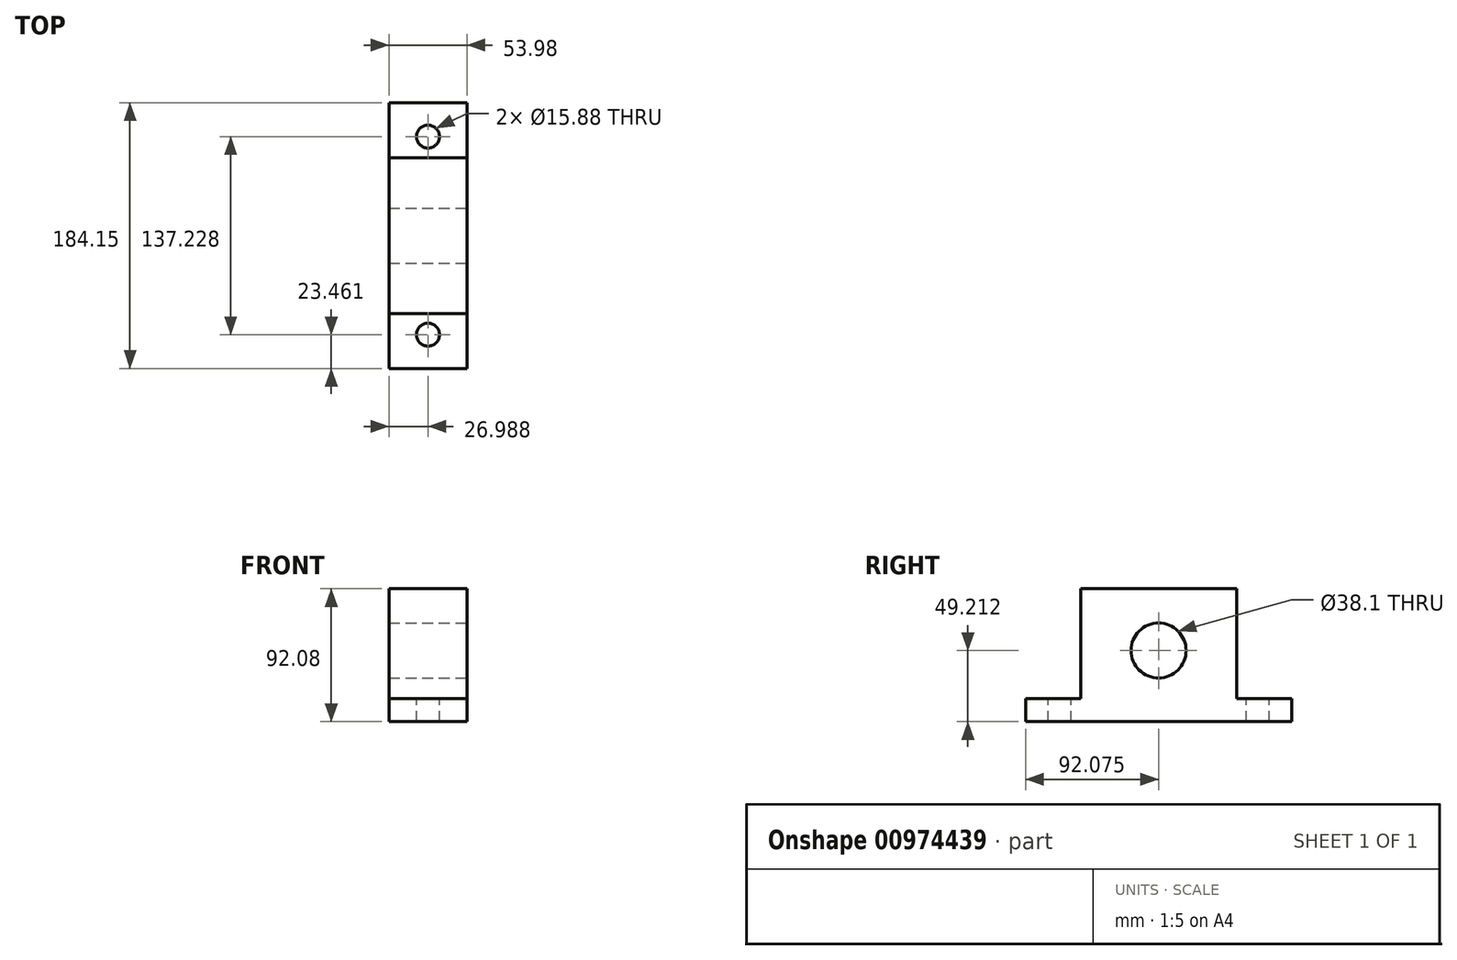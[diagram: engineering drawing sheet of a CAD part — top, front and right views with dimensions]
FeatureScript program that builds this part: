
annotation { "Feature Type Name" : "Feature", "Feature Type Description" : "" }
export const myFeature = defineFeature(function(context is Context, id is Id, definition is map)
    precondition{}
    {
        {
            var Q0;
            Q0=qCreatedBy(makeId("Top.planeOp"),FACE);
            var sketch = newSketch(context, id + "F0", { "sketchPlane" : qUnion([Q0])});
            skLineSegment(sketch, "E0", {"start": v(0, 0) * mm, "end": v(0, 127) * mm});
            skLineSegment(sketch, "E1", {"start": v(0, 127) * mm, "end": v(53.97, 127) * mm});
            skLineSegment(sketch, "E2", {"start": v(53.97, 127) * mm, "end": v(53.97, -57.15) * mm});
            skLineSegment(sketch, "E3", {"start": v(53.97, -57.15) * mm, "end": v(0, -57.15) * mm});
            skLineSegment(sketch, "E4", {"start": v(0, -57.15) * mm, "end": v(0, 0) * mm});
            skSolve(sketch);
        }
        {
            var Q0;
            Q0 = qSketchRegion(id + "F0", true);
            extrude(context, id + "F1", {"entities" : qUnion([Q0]), "depth" : 15.88 * mm, "offsetDistance" : 25.4 * mm});
        }
        {
            var Q0;
            Q0=makeQuery(id+"F1.opExtrude","CAP_FACE",FACE,{"disambiguationData":[OSD([sQuery(id+"F0.wireOp",EDGE,"E0"),sQuery(id+"F0.wireOp",EDGE,"E1"),sQuery(id+"F0.wireOp",EDGE,"E2"),sQuery(id+"F0.wireOp",EDGE,"E3"),sQuery(id+"F0.wireOp",EDGE,"E4")])],"isStart":false});
            var sketch = newSketch(context, id + "F2", { "sketchPlane" : qUnion([Q0])});
            skLineSegment(sketch, "E5", {"start": v(0, 88.9) * mm, "end": v(53.97, 88.9) * mm});
            skLineSegment(sketch, "E6", {"start": v(53.97, 88.9) * mm, "end": v(53.97, -19.05) * mm});
            skLineSegment(sketch, "E7", {"start": v(53.97, -19.05) * mm, "end": v(0, -19.05) * mm});
            skLineSegment(sketch, "E8", {"start": v(0, -19.05) * mm, "end": v(0, 88.9) * mm});
            skSolve(sketch);
        }
        {
            var Q0;
            Q0 = qSketchRegion(id + "F2", true);
            extrude(context, id + "F3", {"entities" : qUnion([Q0]), "operationType" : NewBodyOperationType.ADD, "depth" : 76.2 * mm, "offsetDistance" : 25.4 * mm});
        }
        {
            var Q0;
            Q0=makeQuery(id+"F3.boolean.opBoolean","MERGE",FACE,{"derivedFrom":[makeQuery(id+"F1.opExtrude","SWEPT_FACE",FACE,{"disambiguationData":[OSD([sQuery(id+"F0.wireOp",EDGE,"E2")])]}),makeQuery(id+"F3.opExtrude","SWEPT_FACE",FACE,{"disambiguationData":[OSD([sQuery(id+"F2.wireOp",EDGE,"E6")])]})]});
            var sketch = newSketch(context, id + "F4", { "sketchPlane" : qUnion([Q0])});
            skCircle(sketch, "E9", {"center": v(34.92, 49.21) * mm, "radius": 19.05 * mm});
            skPoint(sketch, "E9.centerSnap0", {"position": v(34.92, 92.08) * mm});
            skSolve(sketch);
        }
        {
            var Q0;
            Q0 = qSketchRegion(id + "F4", true);
            extrude(context, id + "F5", {"entities" : qUnion([Q0]), "operationType" : NewBodyOperationType.REMOVE, "oppositeDirection" : true, "depth" : 76.2 * mm, "offsetDistance" : 25.4 * mm});
        }
        {
            var Q0;
            {var subQ0=sQuery(id+"F0.wireOp",EDGE,"E2");var subQ1=sQuery(id+"F0.wireOp",EDGE,"E1");var subQ2=sQuery(id+"F0.wireOp",EDGE,"E4");var subQ3=sQuery(id+"F0.wireOp",EDGE,"E0");Q0=makeQuery(id+"F3.boolean.opBoolean","SPLIT",FACE,{"disambiguationData":[TD([makeQuery(id+"F1.opExtrude","SWEPT_FACE",FACE,{"disambiguationData":[OSD([subQ1])]})])],"derivedFrom":makeQuery(id+"F1.opExtrude","CAP_FACE",FACE,{"disambiguationData":[OSD([subQ3,subQ1,subQ0,sQuery(id+"F0.wireOp",EDGE,"E3"),subQ2])],"isStart":false})});}
            var sketch = newSketch(context, id + "F6", { "sketchPlane" : qUnion([Q0])});
            skLineSegment(sketch, "E10", {"start": v(26.99, 127) * mm, "end": v(26.99, 103.54) * mm});
            skCircle(sketch, "E11", {"center": v(26.99, 103.54) * mm, "radius": 7.94 * mm});
            skSolve(sketch);
        }
        {
            var Q0;
            Q0 = qSketchRegion(id + "F6", true);
            extrude(context, id + "F7", {"entities" : qUnion([Q0]), "operationType" : NewBodyOperationType.REMOVE, "oppositeDirection" : true, "depth" : 76.2 * mm, "offsetDistance" : 25.4 * mm});
        }
        {
            var Q0;
            {var subQ0=sQuery(id+"F0.wireOp",EDGE,"E2");var subQ1=sQuery(id+"F0.wireOp",EDGE,"E3");var subQ2=sQuery(id+"F0.wireOp",EDGE,"E4");var subQ3=sQuery(id+"F0.wireOp",EDGE,"E0");Q0=makeQuery(id+"F3.boolean.opBoolean","SPLIT",FACE,{"disambiguationData":[TD([makeQuery(id+"F1.opExtrude","SWEPT_FACE",FACE,{"disambiguationData":[OSD([subQ1])]})])],"derivedFrom":makeQuery(id+"F1.opExtrude","CAP_FACE",FACE,{"disambiguationData":[OSD([subQ3,sQuery(id+"F0.wireOp",EDGE,"E1"),subQ0,subQ1,subQ2])],"isStart":false})});}
            var sketch = newSketch(context, id + "F8", { "sketchPlane" : qUnion([Q0])});
            skCircle(sketch, "E12", {"center": v(26.99, -33.69) * mm, "radius": 7.94 * mm});
            skPoint(sketch, "E12.centerSnap0", {"position": v(26.99, -57.15) * mm});
            skSolve(sketch);
        }
        {
            var Q0;
            Q0 = qSketchRegion(id + "F8", true);
            extrude(context, id + "F9", {"entities" : qUnion([Q0]), "operationType" : NewBodyOperationType.REMOVE, "oppositeDirection" : true, "depth" : 25.4 * mm, "offsetDistance" : 25.4 * mm});
        }
    });
